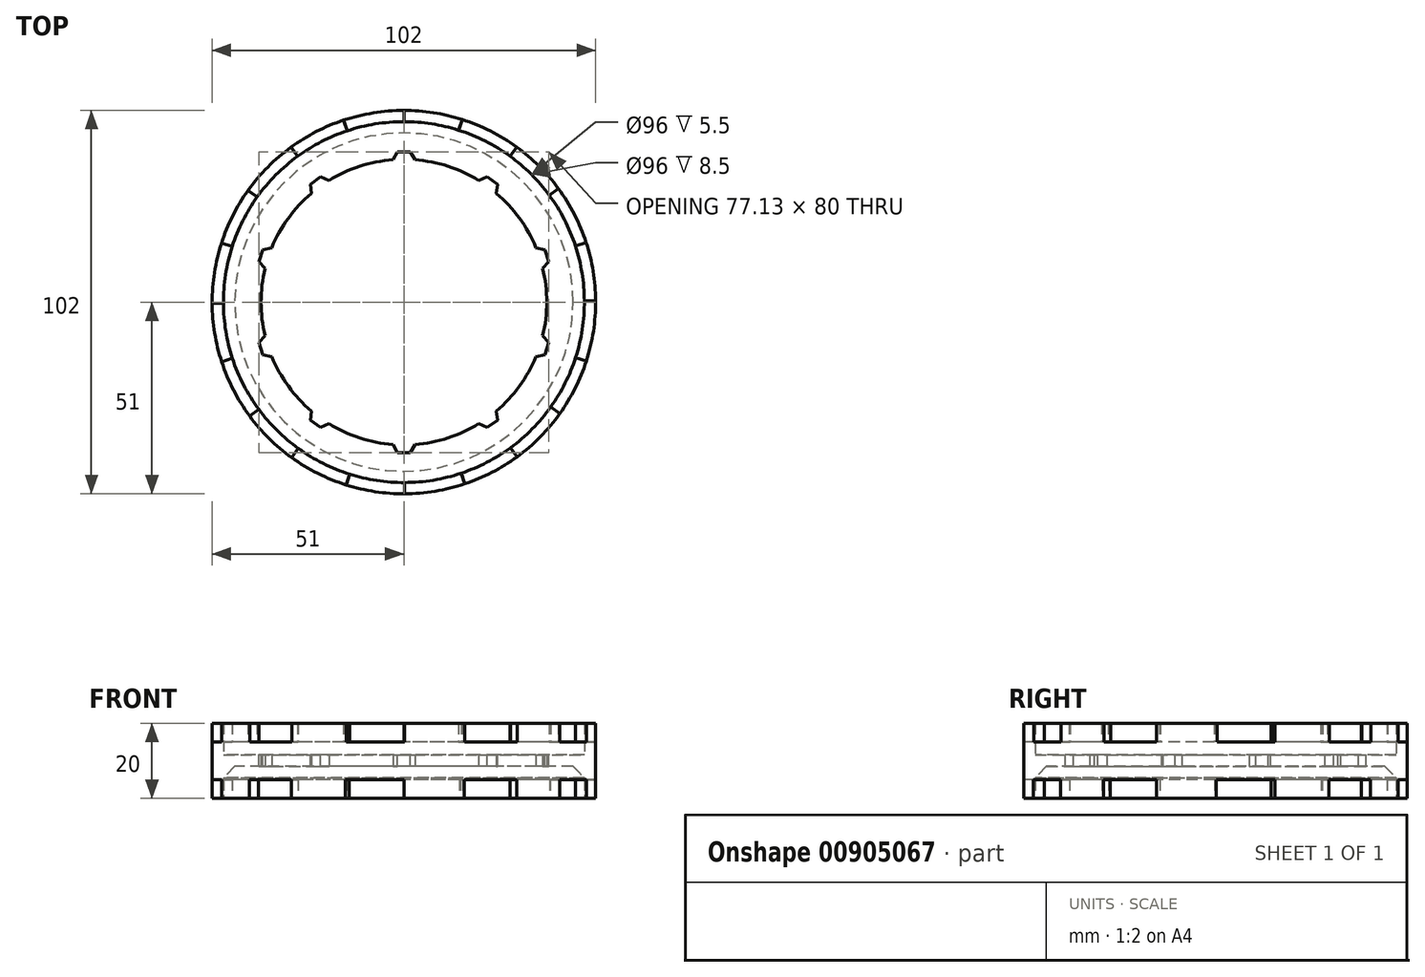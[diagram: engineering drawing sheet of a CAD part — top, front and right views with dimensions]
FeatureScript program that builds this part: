
annotation { "Feature Type Name" : "Feature", "Feature Type Description" : "" }
export const myFeature = defineFeature(function(context is Context, id is Id, definition is map)
    precondition{}
    {
        {
            var Q0;
            Q0=qCreatedBy(makeId("Top.planeOp"),FACE);
            var sketch = newSketch(context, id + "F0", { "sketchPlane" : qUnion([Q0])});
            skCircle(sketch, "E0", {"center": v(0, 0) * mm, "radius": 48 * mm});
            skCircle(sketch, "E1", {"center": v(0, 0) * mm, "radius": 51 * mm});
            skLineSegment(sketch, "E2", {"start": v(48, 0) * mm, "end": v(51, 0) * mm, "construction": true});
            skCircle(sketch, "E3", {"center": v(0, 0) * mm, "radius": 38 * mm});
            skLineSegment(sketch, "E4", {"start": v(38, 0) * mm, "end": v(48, 0) * mm, "construction": true});
            skSolve(sketch);
        }
        {
            var Q0;
            Q0=makeQuery(id+"F0.imprint","IMPRINT",FACE,{"disambiguationData":[TD([[makeQuery(id+"F0.imprint","IMPRINT",EDGE,{"derivedFrom":sQuery(id+"F0.wireOp",EDGE,"E0")}),-1.0]])]});
            extrude(context, id + "F1", {"entities" : qUnion([Q0]), "endBound" : BoundingType.SYMMETRIC, "depth" : 20 * mm, "offsetDistance" : 25 * mm});
        }
        {
            var Q0;
            Q0=makeQuery(id+"F0.imprint","IMPRINT",FACE,{"disambiguationData":[TD([[makeQuery(id+"F0.imprint","IMPRINT",EDGE,{"derivedFrom":sQuery(id+"F0.wireOp",EDGE,"E0")}),1.0]])]});
            extrude(context, id + "F2", {"entities" : qUnion([Q0]), "operationType" : NewBodyOperationType.ADD, "endBound" : BoundingType.SYMMETRIC, "depth" : 3 * mm, "offsetDistance" : 25 * mm});
        }
        {
            var Q0;
            Q0=qCreatedBy(makeId("Top.planeOp"),FACE);
            cPlane(context, id + "F3", {"entities" : qUnion([Q0]), "cplaneType" : CPlaneType.OFFSET, "offset" : 15 * mm, "width" : 150 * mm, "height" : 150 * mm});
        }
        {
            var Q0;
            Q0=qCreatedBy(id+"F3.planeOp",FACE);
            var sketch = newSketch(context, id + "F4", { "sketchPlane" : qUnion([Q0])});
            skCircle(sketch, "E5.0", {"center": v(0, 0) * mm, "radius": 38 * mm, "construction": true});
            skLineSegment(sketch, "E6.bottom", {"start": v(-4, 40) * mm, "end": v(4, 40) * mm, "construction": true});
            skLineSegment(sketch, "E6.top", {"start": v(-4, 36) * mm, "end": v(4, 36) * mm, "construction": true});
            skLineSegment(sketch, "E6.left", {"start": v(-4, 40) * mm, "end": v(-4, 36) * mm, "construction": true});
            skLineSegment(sketch, "E6.right", {"start": v(4, 40) * mm, "end": v(4, 36) * mm, "construction": true});
            skPoint(sketch, "E6.middle", {"position": v(0, 38) * mm});
            skLineSegment(sketch, "E7", {"start": v(-4, 36) * mm, "end": v(-1.7, 40) * mm});
            skLineSegment(sketch, "E8", {"start": v(-1.7, 40) * mm, "end": v(1.7, 40) * mm});
            skLineSegment(sketch, "E9", {"start": v(1.7, 40) * mm, "end": v(4, 36) * mm});
            skLineSegment(sketch, "E10", {"start": v(4, 36) * mm, "end": v(-4, 36) * mm});
            skLineSegment(sketch, "E11.1.0", {"start": v(-20.28, 34.71) * mm, "end": v(-17.92, 31.48) * mm, "construction": true});
            skLineSegment(sketch, "E11.1.1", {"start": v(-24.4, 26.77) * mm, "end": v(-17.92, 31.48) * mm, "construction": true});
            skLineSegment(sketch, "E11.1.2", {"start": v(-22.14, 33.35) * mm, "end": v(-17.92, 31.48) * mm});
            skLineSegment(sketch, "E11.1.3", {"start": v(-26.75, 30) * mm, "end": v(-20.28, 34.71) * mm, "construction": true});
            skPoint(sketch, "E11.1.4", {"position": v(-22.34, 30.74) * mm});
            skLineSegment(sketch, "E11.1.5", {"start": v(-26.75, 30) * mm, "end": v(-24.4, 26.77) * mm, "construction": true});
            skLineSegment(sketch, "E11.1.6", {"start": v(-24.4, 26.77) * mm, "end": v(-24.88, 31.37) * mm});
            skLineSegment(sketch, "E11.1.7", {"start": v(-17.92, 31.48) * mm, "end": v(-24.4, 26.77) * mm});
            skLineSegment(sketch, "E11.1.8", {"start": v(-24.88, 31.37) * mm, "end": v(-22.14, 33.35) * mm});
            skLineSegment(sketch, "E11.2.0", {"start": v(-36.8, 16.16) * mm, "end": v(-33, 14.93) * mm, "construction": true});
            skLineSegment(sketch, "E11.2.1", {"start": v(-35.47, 7.32) * mm, "end": v(-33, 14.93) * mm, "construction": true});
            skLineSegment(sketch, "E11.2.2", {"start": v(-37.52, 13.97) * mm, "end": v(-33, 14.93) * mm});
            skLineSegment(sketch, "E11.2.3", {"start": v(-39.28, 8.56) * mm, "end": v(-36.8, 16.16) * mm, "construction": true});
            skPoint(sketch, "E11.2.4", {"position": v(-36.14, 11.74) * mm});
            skLineSegment(sketch, "E11.2.5", {"start": v(-39.28, 8.56) * mm, "end": v(-35.47, 7.32) * mm, "construction": true});
            skLineSegment(sketch, "E11.2.6", {"start": v(-35.47, 7.32) * mm, "end": v(-38.56, 10.75) * mm});
            skLineSegment(sketch, "E11.2.7", {"start": v(-33, 14.93) * mm, "end": v(-35.47, 7.32) * mm});
            skLineSegment(sketch, "E11.2.8", {"start": v(-38.56, 10.75) * mm, "end": v(-37.52, 13.97) * mm});
            skLineSegment(sketch, "E11.3.0", {"start": v(-39.28, -8.56) * mm, "end": v(-35.47, -7.32) * mm, "construction": true});
            skLineSegment(sketch, "E11.3.1", {"start": v(-33, -14.93) * mm, "end": v(-35.47, -7.32) * mm, "construction": true});
            skLineSegment(sketch, "E11.3.2", {"start": v(-38.56, -10.75) * mm, "end": v(-35.47, -7.32) * mm});
            skLineSegment(sketch, "E11.3.3", {"start": v(-36.8, -16.16) * mm, "end": v(-39.28, -8.56) * mm, "construction": true});
            skPoint(sketch, "E11.3.4", {"position": v(-36.14, -11.74) * mm});
            skLineSegment(sketch, "E11.3.5", {"start": v(-36.8, -16.16) * mm, "end": v(-33, -14.93) * mm, "construction": true});
            skLineSegment(sketch, "E11.3.6", {"start": v(-33, -14.93) * mm, "end": v(-37.52, -13.97) * mm});
            skLineSegment(sketch, "E11.3.7", {"start": v(-35.47, -7.32) * mm, "end": v(-33, -14.93) * mm});
            skLineSegment(sketch, "E11.3.8", {"start": v(-37.52, -13.97) * mm, "end": v(-38.56, -10.75) * mm});
            skLineSegment(sketch, "E11.4.0", {"start": v(-26.75, -30) * mm, "end": v(-24.4, -26.77) * mm, "construction": true});
            skLineSegment(sketch, "E11.4.1", {"start": v(-17.92, -31.48) * mm, "end": v(-24.4, -26.77) * mm, "construction": true});
            skLineSegment(sketch, "E11.4.2", {"start": v(-24.88, -31.37) * mm, "end": v(-24.4, -26.77) * mm});
            skLineSegment(sketch, "E11.4.3", {"start": v(-20.28, -34.71) * mm, "end": v(-26.75, -30) * mm, "construction": true});
            skPoint(sketch, "E11.4.4", {"position": v(-22.34, -30.74) * mm});
            skLineSegment(sketch, "E11.4.5", {"start": v(-20.28, -34.71) * mm, "end": v(-17.92, -31.48) * mm, "construction": true});
            skLineSegment(sketch, "E11.4.6", {"start": v(-17.92, -31.48) * mm, "end": v(-22.14, -33.35) * mm});
            skLineSegment(sketch, "E11.4.7", {"start": v(-24.4, -26.77) * mm, "end": v(-17.92, -31.48) * mm});
            skLineSegment(sketch, "E11.4.8", {"start": v(-22.14, -33.35) * mm, "end": v(-24.88, -31.37) * mm});
            skLineSegment(sketch, "E11.5.0", {"start": v(-4, -40) * mm, "end": v(-4, -36) * mm, "construction": true});
            skLineSegment(sketch, "E11.5.1", {"start": v(4, -36) * mm, "end": v(-4, -36) * mm, "construction": true});
            skLineSegment(sketch, "E11.5.2", {"start": v(-1.7, -40) * mm, "end": v(-4, -36) * mm});
            skLineSegment(sketch, "E11.5.3", {"start": v(4, -40) * mm, "end": v(-4, -40) * mm, "construction": true});
            skPoint(sketch, "E11.5.4", {"position": v(0, -38) * mm});
            skLineSegment(sketch, "E11.5.5", {"start": v(4, -40) * mm, "end": v(4, -36) * mm, "construction": true});
            skLineSegment(sketch, "E11.5.6", {"start": v(4, -36) * mm, "end": v(1.7, -40) * mm});
            skLineSegment(sketch, "E11.5.7", {"start": v(-4, -36) * mm, "end": v(4, -36) * mm});
            skLineSegment(sketch, "E11.5.8", {"start": v(1.7, -40) * mm, "end": v(-1.7, -40) * mm});
            skLineSegment(sketch, "E11.6.0", {"start": v(20.28, -34.71) * mm, "end": v(17.92, -31.48) * mm, "construction": true});
            skLineSegment(sketch, "E11.6.1", {"start": v(24.4, -26.77) * mm, "end": v(17.92, -31.48) * mm, "construction": true});
            skLineSegment(sketch, "E11.6.2", {"start": v(22.14, -33.35) * mm, "end": v(17.92, -31.48) * mm});
            skLineSegment(sketch, "E11.6.3", {"start": v(26.75, -30) * mm, "end": v(20.28, -34.71) * mm, "construction": true});
            skPoint(sketch, "E11.6.4", {"position": v(22.34, -30.74) * mm});
            skLineSegment(sketch, "E11.6.5", {"start": v(26.75, -30) * mm, "end": v(24.4, -26.77) * mm, "construction": true});
            skLineSegment(sketch, "E11.6.6", {"start": v(24.4, -26.77) * mm, "end": v(24.88, -31.37) * mm});
            skLineSegment(sketch, "E11.6.7", {"start": v(17.92, -31.48) * mm, "end": v(24.4, -26.77) * mm});
            skLineSegment(sketch, "E11.6.8", {"start": v(24.88, -31.37) * mm, "end": v(22.14, -33.35) * mm});
            skLineSegment(sketch, "E11.7.0", {"start": v(36.8, -16.16) * mm, "end": v(33, -14.93) * mm, "construction": true});
            skLineSegment(sketch, "E11.7.1", {"start": v(35.47, -7.32) * mm, "end": v(33, -14.93) * mm, "construction": true});
            skLineSegment(sketch, "E11.7.2", {"start": v(37.52, -13.97) * mm, "end": v(33, -14.93) * mm});
            skLineSegment(sketch, "E11.7.3", {"start": v(39.28, -8.56) * mm, "end": v(36.8, -16.16) * mm, "construction": true});
            skPoint(sketch, "E11.7.4", {"position": v(36.14, -11.74) * mm});
            skLineSegment(sketch, "E11.7.5", {"start": v(39.28, -8.56) * mm, "end": v(35.47, -7.32) * mm, "construction": true});
            skLineSegment(sketch, "E11.7.6", {"start": v(35.47, -7.32) * mm, "end": v(38.56, -10.75) * mm});
            skLineSegment(sketch, "E11.7.7", {"start": v(33, -14.93) * mm, "end": v(35.47, -7.32) * mm});
            skLineSegment(sketch, "E11.7.8", {"start": v(38.56, -10.75) * mm, "end": v(37.52, -13.97) * mm});
            skLineSegment(sketch, "E11.8.0", {"start": v(39.28, 8.56) * mm, "end": v(35.47, 7.32) * mm, "construction": true});
            skLineSegment(sketch, "E11.8.1", {"start": v(33, 14.93) * mm, "end": v(35.47, 7.32) * mm, "construction": true});
            skLineSegment(sketch, "E11.8.2", {"start": v(38.56, 10.75) * mm, "end": v(35.47, 7.32) * mm});
            skLineSegment(sketch, "E11.8.3", {"start": v(36.8, 16.16) * mm, "end": v(39.28, 8.56) * mm, "construction": true});
            skPoint(sketch, "E11.8.4", {"position": v(36.14, 11.74) * mm});
            skLineSegment(sketch, "E11.8.5", {"start": v(36.8, 16.16) * mm, "end": v(33, 14.93) * mm, "construction": true});
            skLineSegment(sketch, "E11.8.6", {"start": v(33, 14.93) * mm, "end": v(37.52, 13.97) * mm});
            skLineSegment(sketch, "E11.8.7", {"start": v(35.47, 7.32) * mm, "end": v(33, 14.93) * mm});
            skLineSegment(sketch, "E11.8.8", {"start": v(37.52, 13.97) * mm, "end": v(38.56, 10.75) * mm});
            skLineSegment(sketch, "E11.9.0", {"start": v(26.75, 30) * mm, "end": v(24.4, 26.77) * mm, "construction": true});
            skLineSegment(sketch, "E11.9.1", {"start": v(17.92, 31.48) * mm, "end": v(24.4, 26.77) * mm, "construction": true});
            skLineSegment(sketch, "E11.9.2", {"start": v(24.88, 31.37) * mm, "end": v(24.4, 26.77) * mm});
            skLineSegment(sketch, "E11.9.3", {"start": v(20.28, 34.71) * mm, "end": v(26.75, 30) * mm, "construction": true});
            skPoint(sketch, "E11.9.4", {"position": v(22.34, 30.74) * mm});
            skLineSegment(sketch, "E11.9.5", {"start": v(20.28, 34.71) * mm, "end": v(17.92, 31.48) * mm, "construction": true});
            skLineSegment(sketch, "E11.9.6", {"start": v(17.92, 31.48) * mm, "end": v(22.14, 33.35) * mm});
            skLineSegment(sketch, "E11.9.7", {"start": v(24.4, 26.77) * mm, "end": v(17.92, 31.48) * mm});
            skLineSegment(sketch, "E11.9.8", {"start": v(22.14, 33.35) * mm, "end": v(24.88, 31.37) * mm});
            skSolve(sketch);
        }
        {
            var Q0;
            Q0 = qSketchRegion(id + "F4", true);
            extrude(context, id + "F5", {"entities" : qUnion([Q0]), "operationType" : NewBodyOperationType.REMOVE, "oppositeDirection" : true, "depth" : 25 * mm, "offsetDistance" : 25 * mm});
        }
        {
            var Q0;
            Q0=qCreatedBy(makeId("Top.planeOp"),FACE);
            cPlane(context, id + "F6", {"entities" : qUnion([Q0]), "cplaneType" : CPlaneType.OFFSET, "offset" : 30 * mm, "width" : 150 * mm, "height" : 150 * mm});
        }
        {
            var Q0;
            Q0=qCreatedBy(id+"F6.planeOp",FACE);
            var sketch = newSketch(context, id + "F7", { "sketchPlane" : qUnion([Q0])});
            skCircle(sketch, "E12.0", {"center": v(0, 0.15) * mm, "radius": 55 * mm, "construction": true});
            skCircle(sketch, "E12.1", {"center": v(0.08, 0) * mm, "radius": 35 * mm, "construction": true});
            skLineSegment(sketch, "E13", {"start": v(0, 0.15) * mm, "end": v(0, 55.15) * mm, "construction": true});
            skLineSegment(sketch, "E14", {"start": v(0, 0.15) * mm, "end": v(16.74, 52.54) * mm, "construction": true});
            skArc(sketch, "E15", {"start": v(0, 35) * mm, "mid": v(5.37, 34.58) * mm, "end": v(10.6, 33.35) * mm});
            skArc(sketch, "E16", {"start": v(0, 55.15) * mm, "mid": v(8.47, 54.5) * mm, "end": v(16.74, 52.54) * mm});
            skLineSegment(sketch, "E17", {"start": v(0, 35) * mm, "end": v(0, 55.15) * mm});
            skLineSegment(sketch, "E18", {"start": v(10.6, 33.35) * mm, "end": v(16.74, 52.54) * mm});
            skArc(sketch, "E19.1.0", {"start": v(-20.56, 28.27) * mm, "mid": v(-15.97, 31.09) * mm, "end": v(-11, 33.16) * mm});
            skLineSegment(sketch, "E19.1.1", {"start": v(-11, 33.16) * mm, "end": v(-17.33, 52.3) * mm});
            skLineSegment(sketch, "E19.1.2", {"start": v(-20.56, 28.27) * mm, "end": v(-32.4, 44.57) * mm});
            skArc(sketch, "E19.1.3", {"start": v(-32.4, 44.57) * mm, "mid": v(-25.16, 49.02) * mm, "end": v(-17.33, 52.3) * mm});
            skArc(sketch, "E19.2.0", {"start": v(-33.23, 10.74) * mm, "mid": v(-31.18, 15.71) * mm, "end": v(-28.38, 20.31) * mm});
            skLineSegment(sketch, "E19.2.1", {"start": v(-28.38, 20.31) * mm, "end": v(-44.74, 32.08) * mm});
            skLineSegment(sketch, "E19.2.2", {"start": v(-33.23, 10.74) * mm, "end": v(-52.4, 16.96) * mm});
            skArc(sketch, "E19.2.3", {"start": v(-52.4, 16.96) * mm, "mid": v(-49.15, 24.82) * mm, "end": v(-44.74, 32.08) * mm});
            skArc(sketch, "E19.3.0", {"start": v(-33.18, -10.9) * mm, "mid": v(-34.44, -5.66) * mm, "end": v(-34.88, -0.3) * mm});
            skLineSegment(sketch, "E19.3.1", {"start": v(-34.88, -0.3) * mm, "end": v(-55.03, -0.4) * mm});
            skLineSegment(sketch, "E19.3.2", {"start": v(-33.18, -10.9) * mm, "end": v(-52.34, -17.12) * mm});
            skArc(sketch, "E19.3.3", {"start": v(-52.34, -17.12) * mm, "mid": v(-54.34, -8.86) * mm, "end": v(-55.03, -0.4) * mm});
            skArc(sketch, "E19.4.0", {"start": v(-20.42, -28.36) * mm, "mid": v(-24.52, -24.87) * mm, "end": v(-28.03, -20.8) * mm});
            skLineSegment(sketch, "E19.4.1", {"start": v(-28.03, -20.8) * mm, "end": v(-44.28, -32.72) * mm});
            skLineSegment(sketch, "E19.4.2", {"start": v(-20.42, -28.36) * mm, "end": v(-32.27, -44.67) * mm});
            skArc(sketch, "E19.4.3", {"start": v(-32.27, -44.67) * mm, "mid": v(-38.73, -39.16) * mm, "end": v(-44.28, -32.72) * mm});
            skArc(sketch, "E19.5.0", {"start": v(0.17, -35) * mm, "mid": v(-5.2, -34.58) * mm, "end": v(-10.44, -33.35) * mm});
            skLineSegment(sketch, "E19.5.1", {"start": v(-10.44, -33.35) * mm, "end": v(-16.57, -52.54) * mm});
            skLineSegment(sketch, "E19.5.2", {"start": v(0.17, -35) * mm, "end": v(0.17, -55.15) * mm});
            skArc(sketch, "E19.5.3", {"start": v(0.17, -55.15) * mm, "mid": v(-8.3, -54.5) * mm, "end": v(-16.57, -52.54) * mm});
            skArc(sketch, "E19.6.0", {"start": v(20.72, -28.27) * mm, "mid": v(16.14, -31.09) * mm, "end": v(11.17, -33.16) * mm});
            skLineSegment(sketch, "E19.6.1", {"start": v(11.17, -33.16) * mm, "end": v(17.5, -52.3) * mm});
            skLineSegment(sketch, "E19.6.2", {"start": v(20.72, -28.27) * mm, "end": v(32.57, -44.57) * mm});
            skArc(sketch, "E19.6.3", {"start": v(32.57, -44.57) * mm, "mid": v(25.33, -49.02) * mm, "end": v(17.5, -52.3) * mm});
            skArc(sketch, "E19.7.0", {"start": v(33.4, -10.74) * mm, "mid": v(31.34, -15.71) * mm, "end": v(28.55, -20.31) * mm});
            skLineSegment(sketch, "E19.7.1", {"start": v(28.55, -20.31) * mm, "end": v(44.9, -32.08) * mm});
            skLineSegment(sketch, "E19.7.2", {"start": v(33.4, -10.74) * mm, "end": v(52.56, -16.96) * mm});
            skArc(sketch, "E19.7.3", {"start": v(52.56, -16.96) * mm, "mid": v(49.32, -24.82) * mm, "end": v(44.9, -32.08) * mm});
            skArc(sketch, "E19.8.0", {"start": v(33.34, 10.9) * mm, "mid": v(34.6, 5.66) * mm, "end": v(35.05, 0.3) * mm});
            skLineSegment(sketch, "E19.8.1", {"start": v(35.05, 0.3) * mm, "end": v(55.2, 0.4) * mm});
            skLineSegment(sketch, "E19.8.2", {"start": v(33.34, 10.9) * mm, "end": v(52.5, 17.12) * mm});
            skArc(sketch, "E19.8.3", {"start": v(52.5, 17.12) * mm, "mid": v(54.5, 8.86) * mm, "end": v(55.2, 0.4) * mm});
            skArc(sketch, "E19.9.0", {"start": v(20.59, 28.36) * mm, "mid": v(24.69, 24.87) * mm, "end": v(28.2, 20.8) * mm});
            skLineSegment(sketch, "E19.9.1", {"start": v(28.2, 20.8) * mm, "end": v(44.44, 32.72) * mm});
            skLineSegment(sketch, "E19.9.2", {"start": v(20.59, 28.36) * mm, "end": v(32.43, 44.67) * mm});
            skArc(sketch, "E19.9.3", {"start": v(32.43, 44.67) * mm, "mid": v(38.9, 39.16) * mm, "end": v(44.44, 32.72) * mm});
            skSolve(sketch);
        }
        {
            var Q0;
            Q0 = qSketchRegion(id + "F7", true);
            extrude(context, id + "F8", {"entities" : qUnion([Q0]), "operationType" : NewBodyOperationType.REMOVE, "oppositeDirection" : true, "depth" : 25 * mm, "offsetDistance" : 25 * mm});
        }
        {
            var Q0;
            Q0=qCreatedBy(makeId("Top.planeOp"),FACE);
            cPlane(context, id + "F9", {"entities" : qUnion([Q0]), "cplaneType" : CPlaneType.OFFSET, "offset" : 30 * mm, "oppositeDirection" : true, "width" : 150 * mm, "height" : 150 * mm});
        }
        {
            var Q0;
            Q0=qCreatedBy(id+"F9.planeOp",FACE);
            var sketch = newSketch(context, id + "F10", { "sketchPlane" : qUnion([Q0])});
            skCircle(sketch, "E20.0", {"center": v(0.08, 0) * mm, "radius": 55 * mm, "construction": true});
            skCircle(sketch, "E20.1", {"center": v(0.08, 0.35) * mm, "radius": 35 * mm, "construction": true});
            skLineSegment(sketch, "E21", {"start": v(0.08, 0) * mm, "end": v(0.08, 55) * mm, "construction": true});
            skLineSegment(sketch, "E22", {"start": v(0.08, 0) * mm, "end": v(16.9, 52.36) * mm, "construction": true});
            skArc(sketch, "E23", {"start": v(0.08, 35.35) * mm, "mid": v(5.56, 34.92) * mm, "end": v(10.9, 33.65) * mm});
            skArc(sketch, "E24", {"start": v(0.08, 55) * mm, "mid": v(8.6, 54.34) * mm, "end": v(16.9, 52.36) * mm});
            skLineSegment(sketch, "E25", {"start": v(0.08, 35.35) * mm, "end": v(0.08, 55) * mm});
            skLineSegment(sketch, "E26", {"start": v(10.9, 33.65) * mm, "end": v(16.9, 52.36) * mm});
            skArc(sketch, "E27.1.0", {"start": v(-20.7, 28.6) * mm, "mid": v(-16.02, 31.47) * mm, "end": v(-10.95, 33.58) * mm});
            skLineSegment(sketch, "E27.1.1", {"start": v(-10.95, 33.58) * mm, "end": v(-17.08, 52.25) * mm});
            skLineSegment(sketch, "E27.1.2", {"start": v(-20.7, 28.6) * mm, "end": v(-32.25, 44.5) * mm});
            skArc(sketch, "E27.1.3", {"start": v(-32.25, 44.5) * mm, "mid": v(-24.97, 48.97) * mm, "end": v(-17.08, 52.25) * mm});
            skArc(sketch, "E27.2.0", {"start": v(-33.53, 10.92) * mm, "mid": v(-31.44, 16) * mm, "end": v(-28.58, 20.68) * mm});
            skLineSegment(sketch, "E27.2.1", {"start": v(-28.58, 20.68) * mm, "end": v(-44.52, 32.18) * mm});
            skLineSegment(sketch, "E27.2.2", {"start": v(-33.53, 10.92) * mm, "end": v(-52.23, 17) * mm});
            skArc(sketch, "E27.2.3", {"start": v(-52.23, 17) * mm, "mid": v(-48.96, 24.9) * mm, "end": v(-44.52, 32.18) * mm});
            skArc(sketch, "E27.3.0", {"start": v(-33.53, -10.92) * mm, "mid": v(-34.82, -5.59) * mm, "end": v(-35.26, -0.11) * mm});
            skLineSegment(sketch, "E27.3.1", {"start": v(-35.26, -0.11) * mm, "end": v(-54.92, -0.18) * mm});
            skLineSegment(sketch, "E27.3.2", {"start": v(-33.53, -10.92) * mm, "end": v(-52.23, -17) * mm});
            skArc(sketch, "E27.3.3", {"start": v(-52.23, -17) * mm, "mid": v(-54.23, -8.7) * mm, "end": v(-54.92, -0.18) * mm});
            skArc(sketch, "E27.4.0", {"start": v(-20.7, -28.6) * mm, "mid": v(-24.87, -25.03) * mm, "end": v(-28.45, -20.87) * mm});
            skLineSegment(sketch, "E27.4.1", {"start": v(-28.45, -20.87) * mm, "end": v(-44.3, -32.47) * mm});
            skLineSegment(sketch, "E27.4.2", {"start": v(-20.7, -28.6) * mm, "end": v(-32.25, -44.5) * mm});
            skArc(sketch, "E27.4.3", {"start": v(-32.25, -44.5) * mm, "mid": v(-38.75, -38.95) * mm, "end": v(-44.3, -32.47) * mm});
            skArc(sketch, "E27.5.0", {"start": v(0.08, -35.35) * mm, "mid": v(-5.4, -34.92) * mm, "end": v(-10.73, -33.65) * mm});
            skLineSegment(sketch, "E27.5.1", {"start": v(-10.73, -33.65) * mm, "end": v(-16.74, -52.36) * mm});
            skLineSegment(sketch, "E27.5.2", {"start": v(0.08, -35.35) * mm, "end": v(0.08, -55) * mm});
            skArc(sketch, "E27.5.3", {"start": v(0.08, -55) * mm, "mid": v(-8.43, -54.34) * mm, "end": v(-16.74, -52.36) * mm});
            skArc(sketch, "E27.6.0", {"start": v(20.86, -28.6) * mm, "mid": v(16.18, -31.47) * mm, "end": v(11.11, -33.58) * mm});
            skLineSegment(sketch, "E27.6.1", {"start": v(11.11, -33.58) * mm, "end": v(17.25, -52.25) * mm});
            skLineSegment(sketch, "E27.6.2", {"start": v(20.86, -28.6) * mm, "end": v(32.41, -44.5) * mm});
            skArc(sketch, "E27.6.3", {"start": v(32.41, -44.5) * mm, "mid": v(25.13, -48.96) * mm, "end": v(17.25, -52.25) * mm});
            skArc(sketch, "E27.7.0", {"start": v(33.7, -10.92) * mm, "mid": v(31.6, -16) * mm, "end": v(28.75, -20.68) * mm});
            skLineSegment(sketch, "E27.7.1", {"start": v(28.75, -20.68) * mm, "end": v(44.68, -32.18) * mm});
            skLineSegment(sketch, "E27.7.2", {"start": v(33.7, -10.92) * mm, "end": v(52.4, -17) * mm});
            skArc(sketch, "E27.7.3", {"start": v(52.4, -17) * mm, "mid": v(49.13, -24.9) * mm, "end": v(44.68, -32.18) * mm});
            skArc(sketch, "E27.8.0", {"start": v(33.7, 10.92) * mm, "mid": v(34.98, 5.59) * mm, "end": v(35.43, 0.11) * mm});
            skLineSegment(sketch, "E27.8.1", {"start": v(35.43, 0.11) * mm, "end": v(55.08, 0.18) * mm});
            skLineSegment(sketch, "E27.8.2", {"start": v(33.7, 10.92) * mm, "end": v(52.4, 17) * mm});
            skArc(sketch, "E27.8.3", {"start": v(52.4, 17) * mm, "mid": v(54.4, 8.7) * mm, "end": v(55.08, 0.18) * mm});
            skArc(sketch, "E27.9.0", {"start": v(20.86, 28.6) * mm, "mid": v(25.04, 25.03) * mm, "end": v(28.61, 20.87) * mm});
            skLineSegment(sketch, "E27.9.1", {"start": v(28.61, 20.87) * mm, "end": v(44.47, 32.47) * mm});
            skLineSegment(sketch, "E27.9.2", {"start": v(20.86, 28.6) * mm, "end": v(32.41, 44.5) * mm});
            skArc(sketch, "E27.9.3", {"start": v(32.41, 44.5) * mm, "mid": v(38.91, 38.95) * mm, "end": v(44.47, 32.47) * mm});
            skSolve(sketch);
        }
        {
            var Q0;
            Q0 = qSketchRegion(id + "F10", true);
            extrude(context, id + "F11", {"entities" : qUnion([Q0]), "operationType" : NewBodyOperationType.REMOVE, "depth" : 25 * mm, "offsetDistance" : 25 * mm});
        }
        {
            var Q0;
            Q0=makeQuery(id+"F2.opExtrude","CAP_EDGE",EDGE,{"disambiguationData":[OSD([sQuery(id+"F0.wireOp",EDGE,"E0")])],"isStart":false});
            var Q1;
            Q1=makeQuery(id+"F2.opExtrude","CAP_EDGE",EDGE,{"disambiguationData":[OSD([sQuery(id+"F0.wireOp",EDGE,"E0")])],"isStart":true});
            chamfer(context, id + "F12", {"entities" : qUnion([Q0, Q1]), "width" : 3 * mm, "tangentPropagation" : true});
        }
    });
